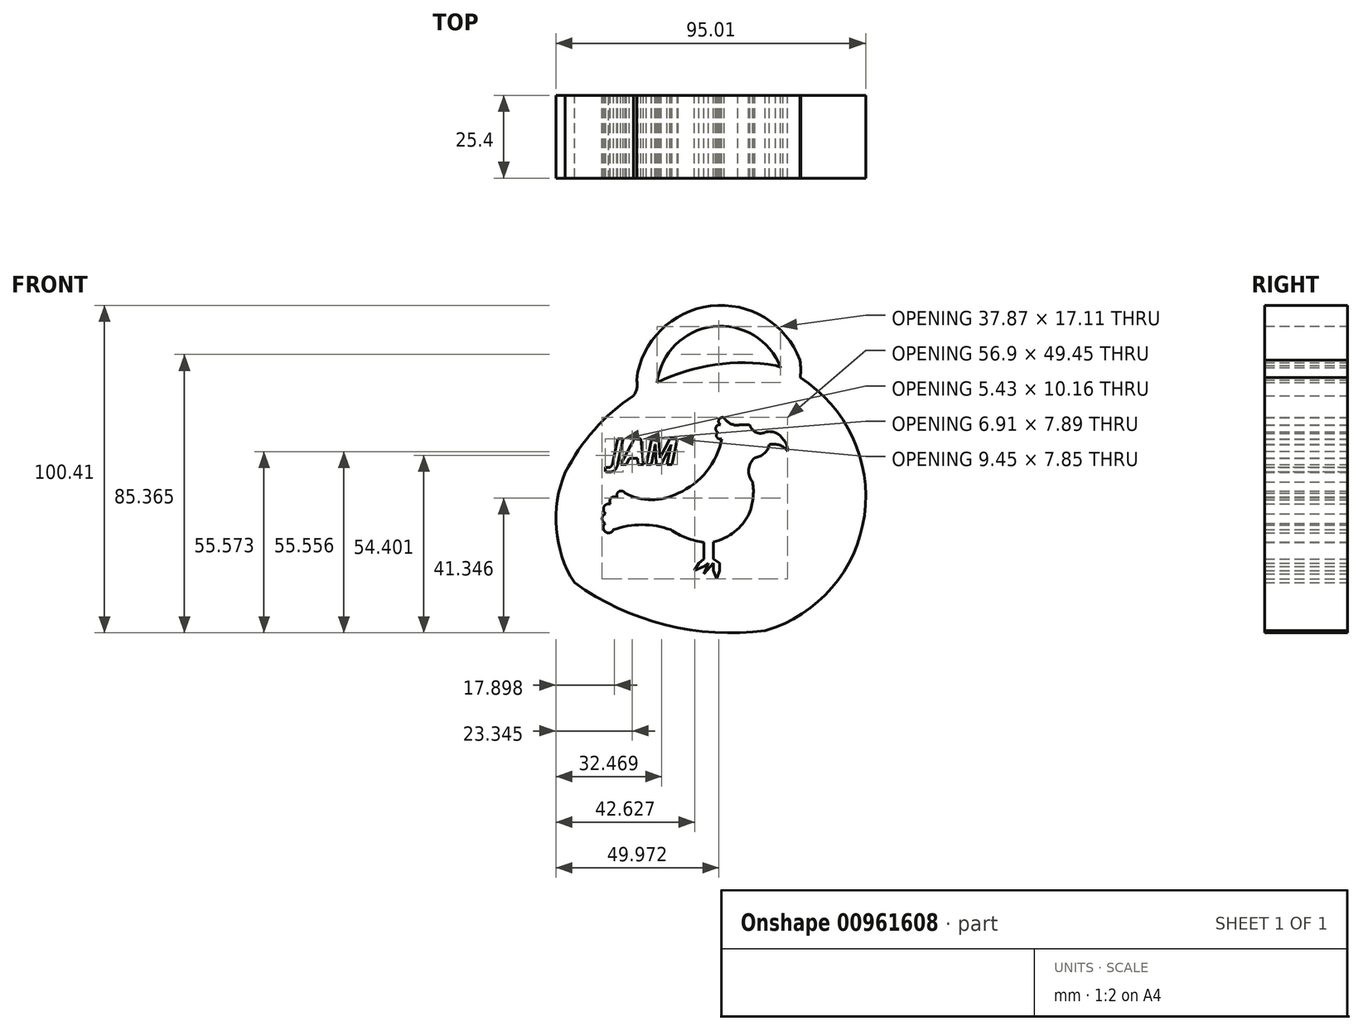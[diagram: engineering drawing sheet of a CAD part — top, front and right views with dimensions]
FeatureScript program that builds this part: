
annotation { "Feature Type Name" : "Feature", "Feature Type Description" : "" }
export const myFeature = defineFeature(function(context is Context, id is Id, definition is map)
    precondition{}
    {
        {
            var Q0;
            Q0=qCreatedBy(makeId("Front.planeOp"),FACE);
            var sketch = newSketch(context, id + "F0", { "sketchPlane" : qUnion([Q0])});
            skArc(sketch, "E0", {"start": v(5.38, 44.06) * mm, "mid": v(3.04, 46) * mm, "end": v(0, 46.19) * mm});
            skArc(sketch, "E1", {"start": v(6.84, 40.34) * mm, "mid": v(6.5, 42.35) * mm, "end": v(5.38, 44.06) * mm});
            skArc(sketch, "E2", {"start": v(6.84, 40.34) * mm, "mid": v(4.35, 42.18) * mm, "end": v(1.26, 42.35) * mm});
            skPoint(sketch, "E2.endSnap0", {"position": v(6.5, 42.35) * mm});
            skArc(sketch, "E3", {"start": v(-3.26, 38.34) * mm, "mid": v(-0.36, 39.62) * mm, "end": v(1.26, 42.35) * mm});
            skArc(sketch, "E4", {"start": v(-4.72, 48.31) * mm, "mid": v(-2.87, 46.11) * mm, "end": v(0, 46.19) * mm});
            skArc(sketch, "E5", {"start": v(-43, 27.45) * mm, "mid": v(-34.89, 25.42) * mm, "end": v(-26.78, 27.45) * mm});
            skArc(sketch, "E6", {"start": v(-43, 27.45) * mm, "mid": v(-45.08, 27.84) * mm, "end": v(-44.99, 25.72) * mm});
            skArc(sketch, "E7", {"start": v(-44.99, 25.72) * mm, "mid": v(-47.47, 25.78) * mm, "end": v(-46.58, 23.46) * mm});
            skArc(sketch, "E8", {"start": v(-46.58, 23.46) * mm, "mid": v(-49.55, 23.08) * mm, "end": v(-47.47, 20.93) * mm});
            skPoint(sketch, "E8.endSnap0", {"position": v(-47.47, 25.78) * mm});
            skArc(sketch, "E9", {"start": v(-47.47, 20.93) * mm, "mid": v(-50.05, 19.67) * mm, "end": v(-47.47, 18.4) * mm});
            skArc(sketch, "E10", {"start": v(-47.47, 18.4) * mm, "mid": v(-49.57, 16.28) * mm, "end": v(-46.58, 16.28) * mm});
            skArc(sketch, "E11", {"start": v(-29.04, 16.28) * mm, "mid": v(-37.81, 17.78) * mm, "end": v(-46.58, 16.28) * mm});
            skArc(sketch, "E12", {"start": v(-29.04, 16.28) * mm, "mid": v(-24.15, 13.75) * mm, "end": v(-18.8, 12.43) * mm});
            skLineSegment(sketch, "E13", {"start": v(-18.8, 12.43) * mm, "end": v(-18.8, 7.24) * mm});
            skLineSegment(sketch, "E14", {"start": v(-18.8, 7.24) * mm, "end": v(-20.4, 6.05) * mm});
            skLineSegment(sketch, "E15", {"start": v(-20.4, 6.05) * mm, "end": v(-21.73, 3.79) * mm});
            skLineSegment(sketch, "E16", {"start": v(-21.73, 3.79) * mm, "end": v(-18.8, 4.98) * mm});
            skLineSegment(sketch, "E17", {"start": v(-18.8, 4.98) * mm, "end": v(-17.48, 6.05) * mm});
            skLineSegment(sketch, "E18", {"start": v(-17.48, 6.05) * mm, "end": v(-18.8, 2.72) * mm});
            skLineSegment(sketch, "E19", {"start": v(-18.8, 2.72) * mm, "end": v(-15.88, 6.05) * mm});
            skLineSegment(sketch, "E20", {"start": v(-15.88, 6.05) * mm, "end": v(-15.88, 3.79) * mm});
            skLineSegment(sketch, "E21", {"start": v(-15.88, 3.79) * mm, "end": v(-14.95, 1.26) * mm});
            skLineSegment(sketch, "E22", {"start": v(-14.95, 1.26) * mm, "end": v(-14.02, 3.79) * mm});
            skLineSegment(sketch, "E23", {"start": v(-14.02, 3.79) * mm, "end": v(-14.02, 6.05) * mm});
            skLineSegment(sketch, "E24", {"start": v(-14.02, 6.05) * mm, "end": v(-15.88, 7.24) * mm});
            skLineSegment(sketch, "E25", {"start": v(-15.88, 7.24) * mm, "end": v(-15.88, 12.56) * mm});
            skArc(sketch, "E26", {"start": v(-15.88, 12.56) * mm, "mid": v(-9.45, 15.64) * mm, "end": v(-4.98, 21.2) * mm});
            skArc(sketch, "E27", {"start": v(-4.98, 21.2) * mm, "mid": v(-3.78, 25.98) * mm, "end": v(-3.92, 30.9) * mm});
            skArc(sketch, "E28", {"start": v(-3.26, 38.34) * mm, "mid": v(-5.1, 34.76) * mm, "end": v(-3.92, 30.9) * mm});
            skArc(sketch, "E29", {"start": v(-4.72, 48.31) * mm, "mid": v(-6.58, 48.47) * mm, "end": v(-8.44, 48.31) * mm});
            skArc(sketch, "E30", {"start": v(-13.36, 46.19) * mm, "mid": v(-10.46, 46.23) * mm, "end": v(-8.44, 48.31) * mm});
            skArc(sketch, "E31", {"start": v(-13.36, 46.19) * mm, "mid": v(-15.02, 45.19) * mm, "end": v(-13.36, 44.2) * mm});
            skArc(sketch, "E32", {"start": v(-13.36, 44.2) * mm, "mid": v(-9.22, 45.15) * mm, "end": v(-6.58, 48.47) * mm});
            skArc(sketch, "E33", {"start": v(-26.78, 27.45) * mm, "mid": v(-18.02, 34.18) * mm, "end": v(-13.36, 44.2) * mm});
            skArc(sketch, "E34", {"start": v(-13.36, 48.31) * mm, "mid": v(-15.24, 47.25) * mm, "end": v(-13.36, 46.19) * mm});
            skArc(sketch, "E35", {"start": v(-13.36, 48.31) * mm, "mid": v(-10.9, 47.83) * mm, "end": v(-8.44, 48.31) * mm});
            skArc(sketch, "E36", {"start": v(-12.67, 50.61) * mm, "mid": v(-10.87, 48.89) * mm, "end": v(-8.44, 48.31) * mm});
            skArc(sketch, "E37", {"start": v(-12.67, 50.61) * mm, "mid": v(-14.3, 49.85) * mm, "end": v(-13.36, 48.31) * mm});
            skArc(sketch, "E38", {"start": v(-15.87, 20.93) * mm, "mid": v(-10.93, 28.44) * mm, "end": v(-13.15, 37.15) * mm});
            skArc(sketch, "E39", {"start": v(-17.74, 22.93) * mm, "mid": v(-18.04, 20.78) * mm, "end": v(-15.87, 20.93) * mm});
            skArc(sketch, "E40", {"start": v(-20.14, 24.65) * mm, "mid": v(-19.8, 22.6) * mm, "end": v(-17.74, 22.93) * mm});
            skArc(sketch, "E41", {"start": v(-21.6, 26.38) * mm, "mid": v(-22.38, 24.24) * mm, "end": v(-20.14, 24.65) * mm});
            skArc(sketch, "E42", {"start": v(-17.02, 33.03) * mm, "mid": v(-19.86, 30.09) * mm, "end": v(-21.6, 26.38) * mm});
            skArc(sketch, "E43", {"start": v(3.12, 66.65) * mm, "mid": v(-34.49, 60.8) * mm, "end": v(-61.34, 33.82) * mm});
            skArc(sketch, "E44", {"start": v(-61.34, 33.82) * mm, "mid": v(-64.1, 16.57) * mm, "end": v(-58.55, 0) * mm});
            skArc(sketch, "E45", {"start": v(-58.55, 0) * mm, "mid": v(-30.66, -12.88) * mm, "end": v(0, -14.69) * mm});
            skArc(sketch, "E46", {"start": v(0, -14.69) * mm, "mid": v(30.75, 24.86) * mm, "end": v(3.12, 66.65) * mm});
            skArc(sketch, "E47", {"start": v(4.68, 66.03) * mm, "mid": v(-16.05, 78.56) * mm, "end": v(-33.2, 61.45) * mm});
            skArc(sketch, "E48.0", {"start": v(10.61, 68.28) * mm, "mid": v(-16.81, 84.86) * mm, "end": v(-39.5, 62.22) * mm});
            skArc(sketch, "E49", {"start": v(-40.46, 57.33) * mm, "mid": v(-39.38, 59.66) * mm, "end": v(-39.5, 62.22) * mm});
            skArc(sketch, "E50", {"start": v(10.61, 62.22) * mm, "mid": v(10.82, 65.25) * mm, "end": v(10.61, 68.28) * mm});
            skText(sketch, "E51", { "text": "JAM", "fontName": "OpenSans-BoldItalic.ttf"});
            const initialGuessF0  = {"E51": [-0.04732, 0.03627, 1, 0, 0.00792]};
            skSetInitialGuess(sketch, initialGuessF0);
            skSolve(sketch);
        }
        {
            var Q0;
            Q0 = qSketchRegion(id + "F0", true);
            extrude(context, id + "F1", {"entities" : qUnion([Q0]), "depth" : 25.4 * mm, "offsetDistance" : 25.4 * mm});
        }
    });
